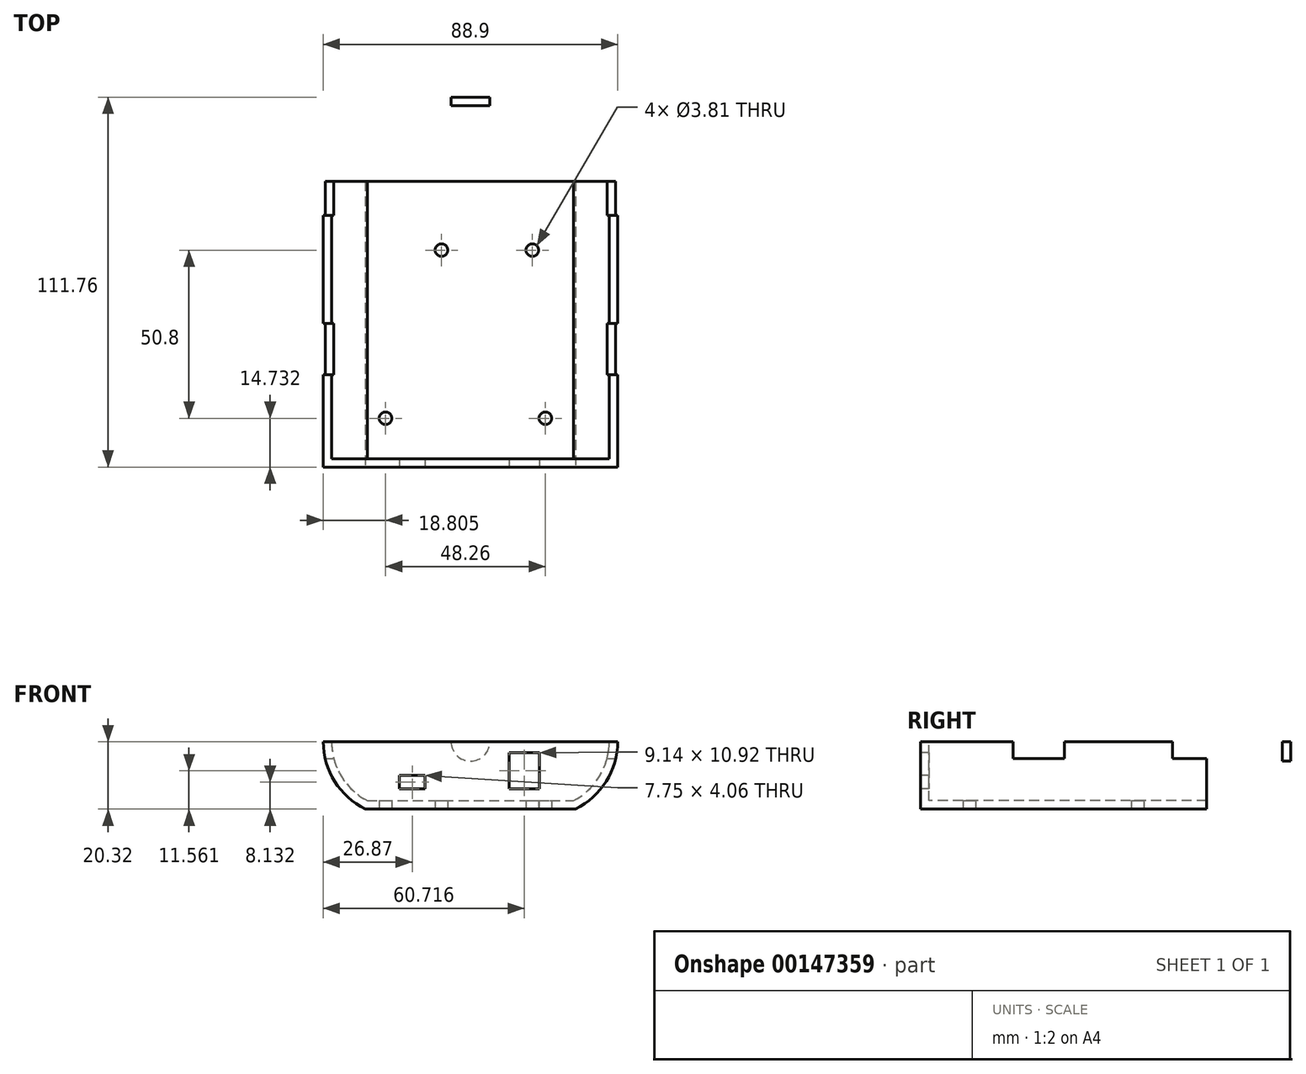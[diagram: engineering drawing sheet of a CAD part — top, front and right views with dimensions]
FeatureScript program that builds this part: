
annotation { "Feature Type Name" : "Feature", "Feature Type Description" : "" }
export const myFeature = defineFeature(function(context is Context, id is Id, definition is map)
    precondition{}
    {
        {
            var Q0;
            Q0=qCreatedBy(makeId("Front.planeOp"),FACE);
            var sketch = newSketch(context, id + "F0", { "sketchPlane" : qUnion([Q0])});
            skLineSegment(sketch, "E0.bottom", {"start": v(-544.15, 315.85) * mm, "end": v(-480.65, 315.85) * mm});
            skArc(sketch, "E1.MirrorCS", {"start": v(-544.15, 315.85) * mm, "mid": v(-553.42, 324.2) * mm, "end": v(-556.85, 336.18) * mm});
            skLineSegment(sketch, "E2.MirrorCS", {"start": v(-467.95, 336.17) * mm, "end": v(-556.85, 336.17) * mm});
            skArc(sketch, "E3.MirrorCS", {"start": v(-467.95, 336.18) * mm, "mid": v(-471.41, 324.22) * mm, "end": v(-480.65, 315.85) * mm});
            skLineSegment(sketch, "E4", {"start": v(-533.85, 321.95) * mm, "end": v(-533.85, 326.01) * mm});
            skLineSegment(sketch, "E5", {"start": v(-533.85, 326.01) * mm, "end": v(-526.1, 326.01) * mm});
            skLineSegment(sketch, "E6", {"start": v(-526.1, 326.01) * mm, "end": v(-526.1, 321.95) * mm});
            skLineSegment(sketch, "E7", {"start": v(-526.1, 321.95) * mm, "end": v(-533.85, 321.95) * mm});
            skLineSegment(sketch, "E8", {"start": v(-500.7, 323.98) * mm, "end": v(-500.7, 321.95) * mm});
            skLineSegment(sketch, "E9", {"start": v(-500.7, 321.95) * mm, "end": v(-491.56, 321.95) * mm});
            skLineSegment(sketch, "E10", {"start": v(-491.56, 321.95) * mm, "end": v(-491.56, 332.87) * mm});
            skLineSegment(sketch, "E11", {"start": v(-491.56, 332.87) * mm, "end": v(-500.7, 332.87) * mm});
            skLineSegment(sketch, "E12", {"start": v(-500.7, 332.87) * mm, "end": v(-500.7, 323.98) * mm});
            skSolve(sketch);
        }
        {
            var Q0;
            {var subQ0=sQuery(id+"F0.wireOp",EDGE,"E0.bottom");Q0=makeQuery(id+"F0.imprint","IMPRINT",FACE,{"disambiguationData":[TD([[makeQuery(id+"F0.imprint","IMPRINT",EDGE,{"derivedFrom":subQ0}),1.0]])]});}
            var Q1;
            Q1=makeQuery(id+"F0.imprint","IMPRINT",FACE,{"disambiguationData":[TD([[makeQuery(id+"F0.imprint","IMPRINT",EDGE,{"derivedFrom":sQuery(id+"F0.wireOp",EDGE,"E4")}),-1.0]])]});
            var Q2;
            Q2=makeQuery(id+"F0.imprint","IMPRINT",FACE,{"disambiguationData":[TD([[makeQuery(id+"F0.imprint","IMPRINT",EDGE,{"derivedFrom":sQuery(id+"F0.wireOp",EDGE,"E8")}),1.0]])]});
            extrude(context, id + "F1", {"entities" : qUnion([Q0, Q1, Q2]), "oppositeDirection" : true, "depth" : 111.76 * mm});
        }
        {
            var Q0;
            Q0=makeQuery(id+"F1.opExtrude","SWEPT_FACE",FACE,{"disambiguationData":[OSD([sQuery(id+"F0.wireOp",EDGE,"E2.MirrorCS")])]});
            shell(context, id + "F2", {"entities" : qUnion([Q0]), "thickness" : 2.54 * mm});
        }
        {
            var Q0;
            Q0=makeQuery(id+"F0.imprint","IMPRINT",FACE,{"disambiguationData":[TD([[makeQuery(id+"F0.imprint","IMPRINT",EDGE,{"derivedFrom":sQuery(id+"F0.wireOp",EDGE,"E4")}),-1.0]])]});
            var Q1;
            Q1=makeQuery(id+"F0.imprint","IMPRINT",FACE,{"disambiguationData":[TD([[makeQuery(id+"F0.imprint","IMPRINT",EDGE,{"derivedFrom":sQuery(id+"F0.wireOp",EDGE,"E8")}),1.0]])]});
            extrude(context, id + "F3", {"entities" : qUnion([Q0, Q1]), "operationType" : NewBodyOperationType.REMOVE, "oppositeDirection" : true, "depth" : 25.4 * mm});
        }
        {
            var Q0;
            Q0=makeQuery(id+"F1.opExtrude","CAP_FACE",FACE,{"disambiguationData":[OSD([sQuery(id+"F0.wireOp",EDGE,"E0.bottom"),sQuery(id+"F0.wireOp",EDGE,"E1.MirrorCS"),sQuery(id+"F0.wireOp",EDGE,"E2.MirrorCS"),sQuery(id+"F0.wireOp",EDGE,"E3.MirrorCS")])],"isStart":false});
            var sketch = newSketch(context, id + "F4", { "sketchPlane" : qUnion([Q0])});
            skLineSegment(sketch, "E13", {"start": v(467.95, 336.17) * mm, "end": v(556.85, 336.17) * mm});
            skArc(sketch, "E14", {"start": v(518.24, 336.17) * mm, "mid": v(512.4, 330.33) * mm, "end": v(506.56, 336.17) * mm});
            skSolve(sketch);
        }
        {
            var Q0;
            {var subQ0=sQuery(id+"F4.wireOp",EDGE,"E14");Q0=makeQuery(id+"F4.imprint","IMPRINT",FACE,{"disambiguationData":[TD([[makeQuery(id+"F4.imprint","IMPRINT",EDGE,{"derivedFrom":subQ0}),-1.0]])]});}
            extrude(context, id + "F5", {"entities" : qUnion([Q0]), "operationType" : NewBodyOperationType.REMOVE, "oppositeDirection" : true, "depth" : 25.4 * mm});
        }
        {
            var Q0;
            Q0=makeQuery(id+"F1.opExtrude","SWEPT_FACE",FACE,{"disambiguationData":[OSD([sQuery(id+"F0.wireOp",EDGE,"E2.MirrorCS")])]});
            var sketch = newSketch(context, id + "F6", { "sketchPlane" : qUnion([Q0])});
            skLineSegment(sketch, "E15", {"start": v(-556.85, 0) * mm, "end": v(-556.85, 111.76) * mm});
            skLineSegment(sketch, "E16", {"start": v(-556.85, 111.76) * mm, "end": v(-556.85, 55.88) * mm});
            skLineSegment(sketch, "E17", {"start": v(-556.85, 55.88) * mm, "end": v(-556.85, 0) * mm});
            skLineSegment(sketch, "E18", {"start": v(-556.85, 83.82) * mm, "end": v(-554.31, 83.82) * mm});
            skLineSegment(sketch, "E19", {"start": v(-467.95, 0) * mm, "end": v(-467.95, 111.76) * mm});
            skLineSegment(sketch, "E20", {"start": v(-467.95, 111.76) * mm, "end": v(-467.95, 55.88) * mm});
            skLineSegment(sketch, "E21", {"start": v(-467.95, 55.88) * mm, "end": v(-467.95, 83.82) * mm});
            skLineSegment(sketch, "E22", {"start": v(-467.95, 83.82) * mm, "end": v(-470.49, 83.82) * mm});
            skLineSegment(sketch, "E23", {"start": v(-467.95, 55.88) * mm, "end": v(-467.95, 0) * mm});
            skLineSegment(sketch, "E24.bottom", {"start": v(-467.95, 27.94) * mm, "end": v(-470.49, 27.94) * mm});
            skLineSegment(sketch, "E24.top", {"start": v(-467.95, 43.43) * mm, "end": v(-470.49, 43.43) * mm});
            skLineSegment(sketch, "E24.left", {"start": v(-467.95, 27.94) * mm, "end": v(-467.95, 43.43) * mm});
            skLineSegment(sketch, "E24.right", {"start": v(-470.49, 27.94) * mm, "end": v(-470.49, 43.43) * mm});
            skLineSegment(sketch, "E25.top", {"start": v(-467.95, 76.07) * mm, "end": v(-470.49, 76.07) * mm});
            skLineSegment(sketch, "E25.left", {"start": v(-467.95, 83.82) * mm, "end": v(-467.95, 76.07) * mm});
            skLineSegment(sketch, "E25.right", {"start": v(-470.49, 83.82) * mm, "end": v(-470.49, 76.07) * mm});
            skLineSegment(sketch, "E26.top", {"start": v(-467.95, 91.57) * mm, "end": v(-470.49, 91.57) * mm});
            skLineSegment(sketch, "E26.left", {"start": v(-467.95, 83.82) * mm, "end": v(-467.95, 91.57) * mm});
            skLineSegment(sketch, "E26.right", {"start": v(-470.49, 83.82) * mm, "end": v(-470.49, 91.57) * mm});
            skLineSegment(sketch, "E27.bottom", {"start": v(-556.85, 27.94) * mm, "end": v(-554.31, 27.94) * mm});
            skLineSegment(sketch, "E27.top", {"start": v(-556.85, 43.43) * mm, "end": v(-554.31, 43.43) * mm});
            skLineSegment(sketch, "E27.left", {"start": v(-556.85, 27.94) * mm, "end": v(-556.85, 43.43) * mm});
            skLineSegment(sketch, "E27.right", {"start": v(-554.31, 27.94) * mm, "end": v(-554.31, 43.43) * mm});
            skLineSegment(sketch, "E28.top", {"start": v(-556.85, 76.07) * mm, "end": v(-554.31, 76.07) * mm});
            skLineSegment(sketch, "E28.left", {"start": v(-556.85, 83.82) * mm, "end": v(-556.85, 76.07) * mm});
            skLineSegment(sketch, "E28.right", {"start": v(-554.31, 83.82) * mm, "end": v(-554.31, 76.07) * mm});
            skLineSegment(sketch, "E29.top", {"start": v(-556.85, 91.57) * mm, "end": v(-554.31, 91.57) * mm});
            skLineSegment(sketch, "E29.left", {"start": v(-556.85, 83.82) * mm, "end": v(-556.85, 91.57) * mm});
            skLineSegment(sketch, "E29.right", {"start": v(-554.31, 83.82) * mm, "end": v(-554.31, 91.57) * mm});
            skSolve(sketch);
        }
        {
            var Q0;
            Q0=makeQuery(id+"F6.imprint","IMPRINT",FACE,{"disambiguationData":[TD([[makeQuery(id+"F6.imprint","IMPRINT",EDGE,{"derivedFrom":sQuery(id+"F6.wireOp",EDGE,"E24.bottom")}),-1.0]])]});
            var Q1;
            Q1=makeQuery(id+"F6.imprint","IMPRINT",FACE,{"disambiguationData":[TD([[makeQuery(id+"F6.imprint","IMPRINT",EDGE,{"derivedFrom":sQuery(id+"F6.wireOp",EDGE,"E25.top")}),-1.0]])]});
            var Q2;
            Q2=makeQuery(id+"F6.imprint","IMPRINT",FACE,{"disambiguationData":[TD([[makeQuery(id+"F6.imprint","IMPRINT",EDGE,{"derivedFrom":sQuery(id+"F6.wireOp",EDGE,"E22")}),-1.0]])]});
            var Q3;
            Q3=makeQuery(id+"F6.imprint","IMPRINT",FACE,{"disambiguationData":[TD([[makeQuery(id+"F6.imprint","IMPRINT",EDGE,{"derivedFrom":sQuery(id+"F6.wireOp",EDGE,"E18")}),1.0]])]});
            var Q4;
            Q4=makeQuery(id+"F6.imprint","IMPRINT",FACE,{"disambiguationData":[TD([[makeQuery(id+"F6.imprint","IMPRINT",EDGE,{"derivedFrom":sQuery(id+"F6.wireOp",EDGE,"E28.top")}),1.0]])]});
            var Q5;
            Q5=makeQuery(id+"F6.imprint","IMPRINT",FACE,{"disambiguationData":[TD([[makeQuery(id+"F6.imprint","IMPRINT",EDGE,{"derivedFrom":sQuery(id+"F6.wireOp",EDGE,"E27.bottom")}),1.0]])]});
            extrude(context, id + "F7", {"entities" : qUnion([Q0, Q1, Q2, Q3, Q4, Q5]), "operationType" : NewBodyOperationType.REMOVE, "oppositeDirection" : true, "depth" : 5.08 * mm});
        }
        {
            var Q0;
            Q0=makeQuery(id+"F1.opExtrude","SWEPT_FACE",FACE,{"disambiguationData":[OSD([sQuery(id+"F0.wireOp",EDGE,"E0.bottom")])]});
            var sketch = newSketch(context, id + "F8", { "sketchPlane" : qUnion([Q0])});
            skLineSegment(sketch, "E30", {"start": v(-533.98, 0) * mm, "end": v(-533.98, -14.73) * mm});
            skLineSegment(sketch, "E31", {"start": v(-533.98, -14.73) * mm, "end": v(-538.05, -14.73) * mm});
            skCircle(sketch, "E32", {"center": v(-538.05, -14.73) * mm, "radius": 1.9 * mm});
            skLineSegment(sketch, "E33", {"start": v(-538.05, -14.73) * mm, "end": v(-489.79, -14.73) * mm});
            skCircle(sketch, "E34", {"center": v(-489.79, -14.73) * mm, "radius": 1.9 * mm});
            skLineSegment(sketch, "E35", {"start": v(-489.79, -14.73) * mm, "end": v(-489.79, -65.53) * mm});
            skLineSegment(sketch, "E36", {"start": v(-489.79, -65.53) * mm, "end": v(-493.72, -65.53) * mm});
            skCircle(sketch, "E37", {"center": v(-493.72, -65.53) * mm, "radius": 1.9 * mm});
            skLineSegment(sketch, "E38", {"start": v(-493.72, -65.53) * mm, "end": v(-521.15, -65.53) * mm});
            skCircle(sketch, "E39", {"center": v(-521.15, -65.53) * mm, "radius": 1.9 * mm});
            skSolve(sketch);
        }
        {
            var Q0;
            Q0=makeQuery(id+"F8.imprint","IMPRINT",FACE,{"disambiguationData":[TD([[makeQuery(id+"F8.imprint","IMPRINT",EDGE,{"derivedFrom":sQuery(id+"F8.wireOp",EDGE,"E32")}),1.0]])]});
            var Q1;
            {var subQ0=sQuery(id+"F8.wireOp",EDGE,"E35");var subQ1=sQuery(id+"F8.wireOp",EDGE,"E33");var subQ2=makeQuery(id+"F8.imprint","INTERSECT",VERTEX,{"derivedFrom":[subQ1,subQ0]});Q1=makeQuery(id+"F8.imprint","IMPRINT",FACE,{"disambiguationData":[TD([[makeQuery(id+"F8.imprint","IMPRINT",EDGE,{"disambiguationData":[TD([[subQ2,1.0]])],"derivedFrom":subQ1}),1.0]])]});}
            var Q2;
            {var subQ0=sQuery(id+"F8.wireOp",EDGE,"E35");var subQ1=sQuery(id+"F8.wireOp",EDGE,"E33");var subQ2=makeQuery(id+"F8.imprint","INTERSECT",VERTEX,{"derivedFrom":[subQ1,subQ0]});Q2=makeQuery(id+"F8.imprint","IMPRINT",FACE,{"disambiguationData":[TD([[makeQuery(id+"F8.imprint","IMPRINT",EDGE,{"disambiguationData":[TD([[subQ2,1.0]])],"derivedFrom":subQ1}),-1.0]])]});}
            var Q3;
            {var subQ0=sQuery(id+"F8.wireOp",EDGE,"E38");var subQ1=sQuery(id+"F8.wireOp",EDGE,"E36");var subQ2=makeQuery(id+"F8.imprint","INTERSECT",VERTEX,{"derivedFrom":[subQ1,subQ0]});Q3=makeQuery(id+"F8.imprint","IMPRINT",FACE,{"disambiguationData":[TD([[makeQuery(id+"F8.imprint","IMPRINT",EDGE,{"disambiguationData":[TD([[subQ2,1.0]])],"derivedFrom":subQ1}),-1.0]])]});}
            var Q4;
            {var subQ0=sQuery(id+"F8.wireOp",EDGE,"E38");var subQ1=sQuery(id+"F8.wireOp",EDGE,"E36");var subQ2=makeQuery(id+"F8.imprint","INTERSECT",VERTEX,{"derivedFrom":[subQ1,subQ0]});Q4=makeQuery(id+"F8.imprint","IMPRINT",FACE,{"disambiguationData":[TD([[makeQuery(id+"F8.imprint","IMPRINT",EDGE,{"disambiguationData":[TD([[subQ2,1.0]])],"derivedFrom":subQ1}),1.0]])]});}
            var Q5;
            Q5=makeQuery(id+"F8.imprint","IMPRINT",FACE,{"disambiguationData":[TD([[makeQuery(id+"F8.imprint","IMPRINT",EDGE,{"derivedFrom":sQuery(id+"F8.wireOp",EDGE,"E39")}),1.0]])]});
            extrude(context, id + "F9", {"entities" : qUnion([Q0, Q1, Q2, Q3, Q4, Q5]), "operationType" : NewBodyOperationType.REMOVE, "oppositeDirection" : true, "depth" : 25.4 * mm});
        }
        {
            var Q0;
            Q0=makeQuery(id+"F7.boolean.opBoolean","COPY",FACE,{"derivedFrom":makeQuery(id+"F7.opExtrude","SWEPT_FACE",FACE,{"disambiguationData":[OSD([sQuery(id+"F6.wireOp",EDGE,"E28.right"),sQuery(id+"F6.wireOp",EDGE,"E29.right")])]})});
            var Q1;
            Q1=makeQuery(id+"F7.boolean.opBoolean","COPY",FACE,{"derivedFrom":makeQuery(id+"F7.opExtrude","SWEPT_FACE",FACE,{"disambiguationData":[OSD([sQuery(id+"F6.wireOp",EDGE,"E27.right")])]})});
            extrude(context, id + "F10", {"entities" : qUnion([Q0, Q1]), "operationType" : NewBodyOperationType.REMOVE, "oppositeDirection" : true, "depth" : 25.4 * mm});
        }
        {
            var Q0;
            Q0=makeQuery(id+"F7.boolean.opBoolean","COPY",FACE,{"derivedFrom":makeQuery(id+"F7.opExtrude","SWEPT_FACE",FACE,{"disambiguationData":[OSD([sQuery(id+"F6.wireOp",EDGE,"E24.right")])]})});
            var Q1;
            Q1=makeQuery(id+"F7.boolean.opBoolean","COPY",FACE,{"derivedFrom":makeQuery(id+"F7.opExtrude","SWEPT_FACE",FACE,{"disambiguationData":[OSD([sQuery(id+"F6.wireOp",EDGE,"E25.right"),sQuery(id+"F6.wireOp",EDGE,"E26.right")])]})});
            extrude(context, id + "F11", {"entities" : qUnion([Q0, Q1]), "operationType" : NewBodyOperationType.REMOVE, "oppositeDirection" : true, "depth" : 25.4 * mm});
        }
        {
            var Q0;
            Q0=makeQuery(id+"F1.opExtrude","SWEPT_BODY",BODY,{"disambiguationData":[OSD([sQuery(id+"F0.wireOp",EDGE,"E0.bottom"),sQuery(id+"F0.wireOp",EDGE,"E1.MirrorCS"),sQuery(id+"F0.wireOp",EDGE,"E2.MirrorCS"),sQuery(id+"F0.wireOp",EDGE,"E3.MirrorCS")])]});
            transform(context, id + "F12", {"entities" : qUnion([Q0]), "transformType" : TransformType.TRANSLATION_3D, "dx" : 0 * mm, "dy" : 0 * mm, "dz" : 0 * mm, "makeCopy" : true});
        }
        {
            var Q0;
            Q0=makeQuery(id+"F12.opPattern","COPY",BODY,{"derivedFrom":makeQuery(id+"F1.opExtrude","SWEPT_BODY",BODY,{"disambiguationData":[OSD([sQuery(id+"F0.wireOp",EDGE,"E0.bottom"),sQuery(id+"F0.wireOp",EDGE,"E1.MirrorCS"),sQuery(id+"F0.wireOp",EDGE,"E2.MirrorCS"),sQuery(id+"F0.wireOp",EDGE,"E3.MirrorCS")])]}),"instanceName":"1"});
            deleteBodies(context, id + "F13", {"entities" : qUnion([Q0])});
        }
        {
            var Q0;
            Q0=makeQuery(id+"F1.opExtrude","SWEPT_BODY",BODY,{"disambiguationData":[OSD([sQuery(id+"F0.wireOp",EDGE,"E0.bottom"),sQuery(id+"F0.wireOp",EDGE,"E1.MirrorCS"),sQuery(id+"F0.wireOp",EDGE,"E2.MirrorCS"),sQuery(id+"F0.wireOp",EDGE,"E3.MirrorCS")])]});
            transform(context, id + "F14", {"entities" : qUnion([Q0]), "transformType" : TransformType.TRANSLATION_3D, "dx" : 0 * mm, "dy" : 0 * mm, "dz" : 0 * mm, "makeCopy" : true});
        }
        {
            var Q0;
            Q0=makeQuery(id+"F14.opPattern","COPY",BODY,{"derivedFrom":makeQuery(id+"F1.opExtrude","SWEPT_BODY",BODY,{"disambiguationData":[OSD([sQuery(id+"F0.wireOp",EDGE,"E0.bottom"),sQuery(id+"F0.wireOp",EDGE,"E1.MirrorCS"),sQuery(id+"F0.wireOp",EDGE,"E2.MirrorCS"),sQuery(id+"F0.wireOp",EDGE,"E3.MirrorCS")])]}),"instanceName":"1"});
            deleteBodies(context, id + "F15", {"entities" : qUnion([Q0])});
        }
    });
